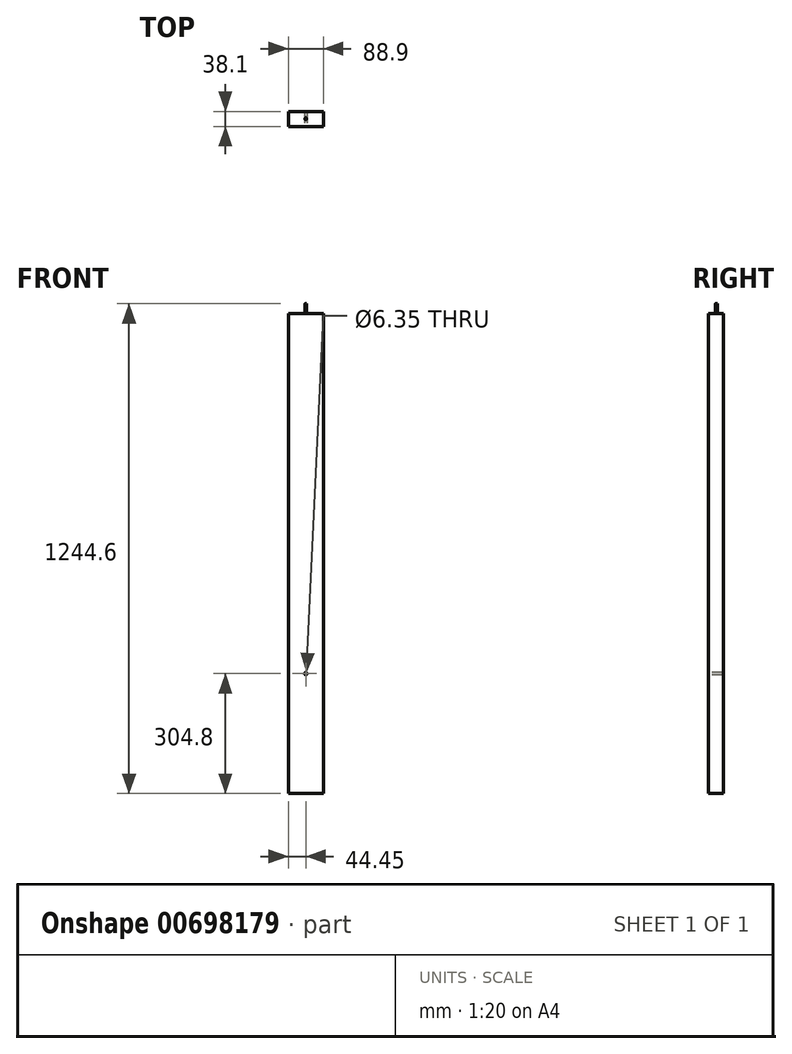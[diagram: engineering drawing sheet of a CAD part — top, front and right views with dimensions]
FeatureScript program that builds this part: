
annotation { "Feature Type Name" : "Feature", "Feature Type Description" : "" }
export const myFeature = defineFeature(function(context is Context, id is Id, definition is map)
    precondition{}
    {
        {
            var Q0;
            Q0=qCreatedBy(makeId("Front.planeOp"),FACE);
            var sketch = newSketch(context, id + "F0", { "sketchPlane" : qUnion([Q0])});
            skLineSegment(sketch, "E0.bottom", {"start": v(0, 0) * mm, "end": v(-88.9, 0) * mm});
            skLineSegment(sketch, "E0.top", {"start": v(0, 1219.2) * mm, "end": v(-88.9, 1219.2) * mm});
            skLineSegment(sketch, "E0.left", {"start": v(0, 0) * mm, "end": v(0, 1219.2) * mm});
            skLineSegment(sketch, "E0.right", {"start": v(-88.9, 0) * mm, "end": v(-88.9, 1219.2) * mm});
            skSolve(sketch);
        }
        {
            var Q0;
            Q0 = qSketchRegion(id + "F0", true);
            extrude(context, id + "F1", {"entities" : qUnion([Q0]), "depth" : 38.1 * mm, "offsetDistance" : 25.4 * mm});
        }
        {
            var Q0;
            Q0=makeQuery(id+"F1.opExtrude","CAP_FACE",FACE,{"disambiguationData":[OSD([sQuery(id+"F0.wireOp",EDGE,"E0.bottom"),sQuery(id+"F0.wireOp",EDGE,"E0.top"),sQuery(id+"F0.wireOp",EDGE,"E0.left"),sQuery(id+"F0.wireOp",EDGE,"E0.right")])],"isStart":false});
            var sketch = newSketch(context, id + "F2", { "sketchPlane" : qUnion([Q0])});
            skPoint(sketch, "E1", {"position": v(-44.45, 304.8) * mm});
            skSolve(sketch);
        }
        {
            var Q0;
            Q0=sQuery(id+"F2.wireOp",VERTEX,"E1");
            var Q1;
            Q1=makeQuery(id+"F1.opExtrude","SWEPT_BODY",BODY,{"disambiguationData":[OSD([sQuery(id+"F0.wireOp",EDGE,"E0.bottom"),sQuery(id+"F0.wireOp",EDGE,"E0.top"),sQuery(id+"F0.wireOp",EDGE,"E0.left"),sQuery(id+"F0.wireOp",EDGE,"E0.right")])]});
            hole(context, id + "F3", {"style" : HoleStyle.SIMPLE, "endStyle" : HoleEndStyle.THROUGH, "holeDiameter" : 6.35 * mm, "majorDiameter" : 6.35 * mm, "isTappedThrough" : true, "tappedDepth" : 12.7 * mm, "tapClearance" : 3, "locations" : qUnion([Q0]), "scope" : qUnion([Q1])});
        }
        {
            var Q0;
            Q0=makeQuery(id+"F1.opExtrude","SWEPT_FACE",FACE,{"disambiguationData":[OSD([sQuery(id+"F0.wireOp",EDGE,"E0.top")])]});
            var sketch = newSketch(context, id + "F4", { "sketchPlane" : qUnion([Q0])});
            skCircle(sketch, "E2", {"center": v(-44.45, -18.4) * mm, "radius": 2.54 * mm});
            skPoint(sketch, "E2.centerSnap0", {"position": v(-44.45, 0) * mm});
            skSolve(sketch);
        }
        {
            var Q0;
            Q0 = qSketchRegion(id + "F4", true);
            extrude(context, id + "F5", {"entities" : qUnion([Q0]), "operationType" : NewBodyOperationType.ADD, "depth" : 25.4 * mm, "offsetDistance" : 25.4 * mm});
        }
    });
